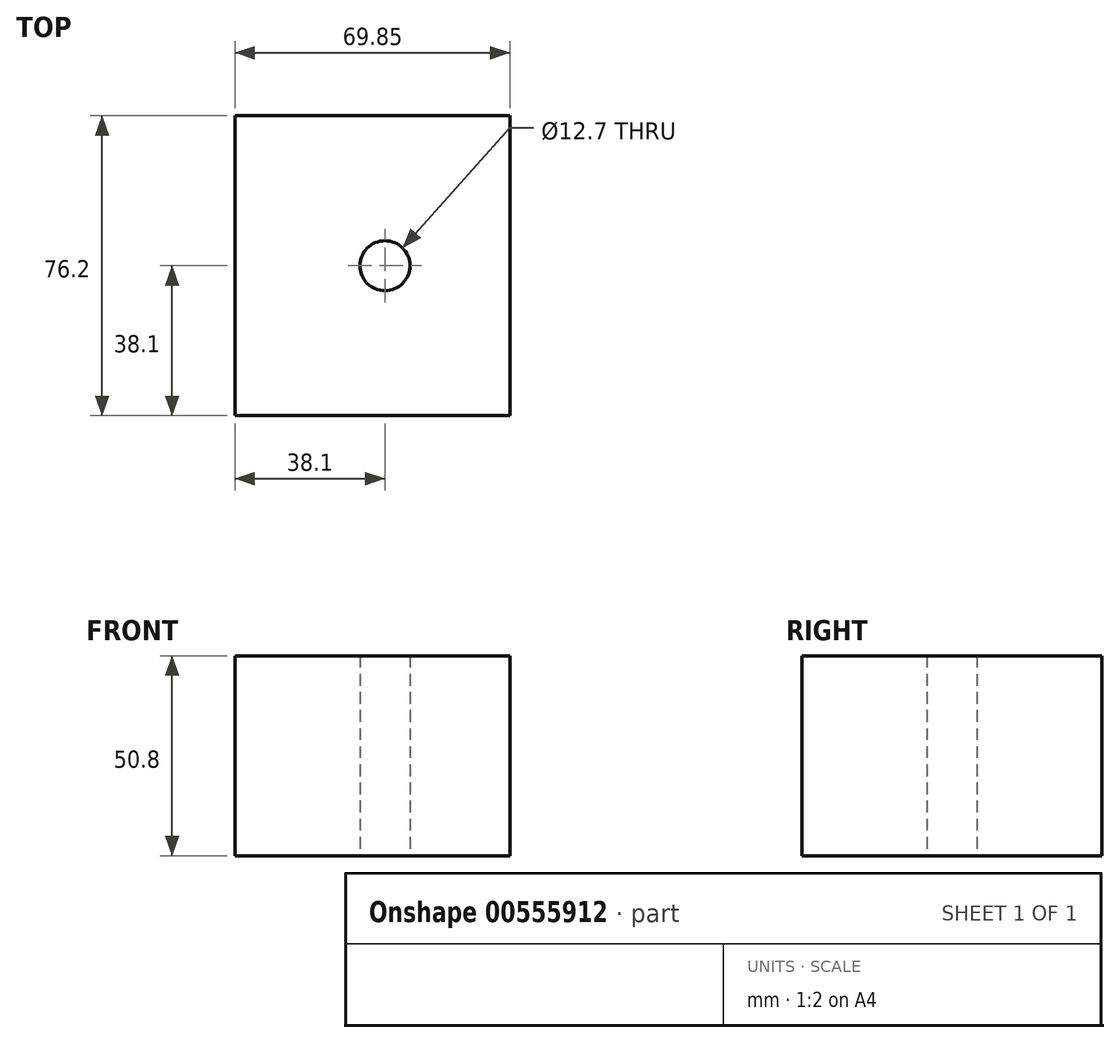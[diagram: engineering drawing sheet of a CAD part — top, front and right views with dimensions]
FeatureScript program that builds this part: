
annotation { "Feature Type Name" : "Feature", "Feature Type Description" : "" }
export const myFeature = defineFeature(function(context is Context, id is Id, definition is map)
    precondition{}
    {
        {
            var Q0;
            Q0=qCreatedBy(makeId("Top.planeOp"),FACE);
            var sketch = newSketch(context, id + "F0", { "sketchPlane" : qUnion([Q0])});
            skLineSegment(sketch, "E0.bottom", {"start": v(0, 0) * mm, "end": v(69.85, 0) * mm});
            skLineSegment(sketch, "E0.top", {"start": v(0, 76.2) * mm, "end": v(69.85, 76.2) * mm});
            skLineSegment(sketch, "E0.left", {"start": v(0, 0) * mm, "end": v(0, 76.2) * mm});
            skLineSegment(sketch, "E0.right", {"start": v(69.85, 0) * mm, "end": v(69.85, 76.2) * mm});
            skCircle(sketch, "E1", {"center": v(38.1, 38.1) * mm, "radius": 6.35 * mm});
            skSolve(sketch);
        }
        {
            var Q0;
            Q0=makeQuery(id+"F0.imprint","IMPRINT",FACE,{"disambiguationData":[TD([[makeQuery(id+"F0.imprint","IMPRINT",EDGE,{"derivedFrom":sQuery(id+"F0.wireOp",EDGE,"E0.bottom")}),1.0]])]});
            extrude(context, id + "F1", {"entities" : qUnion([Q0]), "depth" : 50.8 * mm, "offsetDistance" : 25.4 * mm});
        }
    });
